# Revit family: Papa f-275
name_source: partatom
category: Мебель
revit_build: Autodesk Revit 2017 (Build: 20160225_1515(x64)
units: mm (PartAtom-declared; Revit-internal decimal feet)

## family parameters
Всегда вертикально = Да
Заголовок OmniClass = General Furniture and Specialties
На основе рабочей плоскости = Нет
Номер OmniClass = 23.40.20.00
Общий = Нет
При загрузке вырезать с полостями = Нет
Точка расчета площади = Нет

## types (2) — shared parameters
Chair = Skandiform Wood Oak
Seat = Skandiform Fabric
Группа модели = F-275
Изготовитель = Skandiform AB
Ключевая пометка = XBE.3
Комментарии к типоразмеру = Created by Astacus AB
Описание = Easy-chair in ash or oak, all in wood or with upholstered seat or with upholstered seat and back.

## per-type parameters (varying)
| type | Dyna | URL |
| F-276 | Да | http://file-system.ru |
| F-275 | Нет | http://www.biminfo.se |

## geometry (parser evidence)
native form markers: Blend x30, Sweep x3
no freeform markers — native parametric forms only
